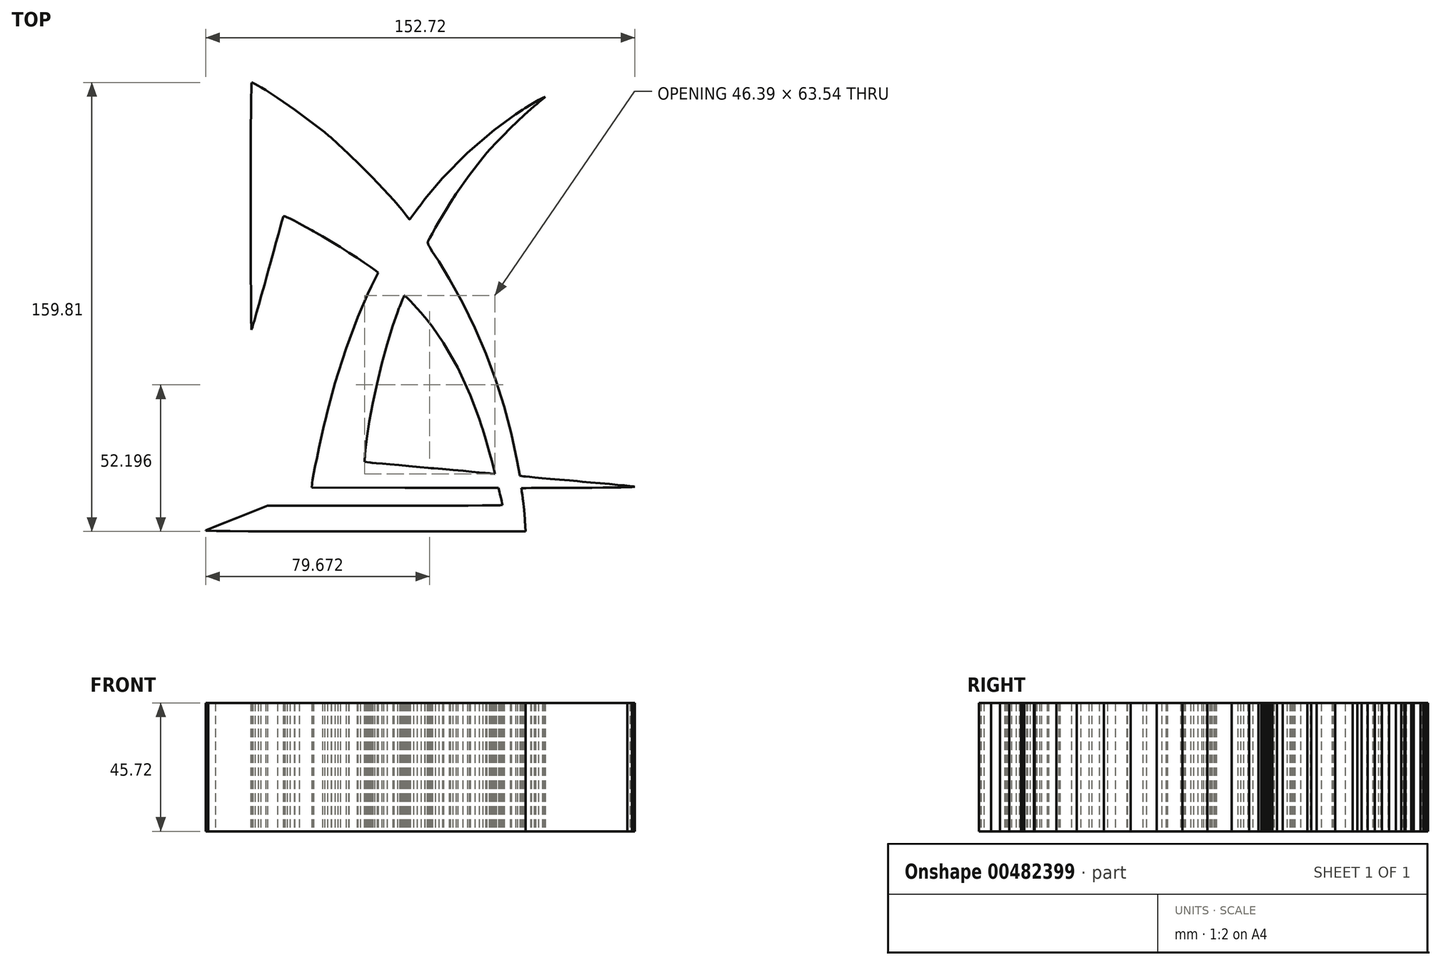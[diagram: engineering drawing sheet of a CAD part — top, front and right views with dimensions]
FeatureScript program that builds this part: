
annotation { "Feature Type Name" : "Feature", "Feature Type Description" : "" }
export const myFeature = defineFeature(function(context is Context, id is Id, definition is map)
    precondition{}
    {
        {
            var Q0;
            Q0=qCreatedBy(makeId("Top.planeOp"),FACE);
            var sketch = newSketch(context, id + "F0", { "sketchPlane" : qUnion([Q0])});
            skLineSegment(sketch, "E0", {"start": v(-90.31, 0) * mm, "end": v(-90.31, -90.31) * mm});
            skLineSegment(sketch, "E1", {"start": v(-90.31, -90.31) * mm, "end": v(90.31, -90.31) * mm});
            skLineSegment(sketch, "E2", {"start": v(90.31, -90.31) * mm, "end": v(90.31, 90.31) * mm});
            skLineSegment(sketch, "E3", {"start": v(90.31, 90.31) * mm, "end": v(-90.31, 90.31) * mm});
            skLineSegment(sketch, "E4", {"start": v(-90.31, 90.31) * mm, "end": v(-90.31, 0) * mm});
            skLineSegment(sketch, "E5", {"start": v(-57.9, 75.78) * mm, "end": v(-56.43, 74.9) * mm});
            skLineSegment(sketch, "E6", {"start": v(-56.43, 74.9) * mm, "end": v(-52.15, 72.16) * mm});
            skLineSegment(sketch, "E7", {"start": v(-52.15, 72.16) * mm, "end": v(-46.09, 67.98) * mm});
            skLineSegment(sketch, "E8", {"start": v(-46.09, 67.98) * mm, "end": v(-39.97, 63.43) * mm});
            skLineSegment(sketch, "E9", {"start": v(-39.97, 63.43) * mm, "end": v(-35.5, 59.91) * mm});
            skLineSegment(sketch, "E10", {"start": v(-35.5, 59.91) * mm, "end": v(-34.04, 58.7) * mm});
            skLineSegment(sketch, "E11", {"start": v(-34.04, 58.7) * mm, "end": v(-33.2, 58) * mm});
            skLineSegment(sketch, "E12", {"start": v(-33.2, 58) * mm, "end": v(-30.73, 55.82) * mm});
            skLineSegment(sketch, "E13", {"start": v(-30.73, 55.82) * mm, "end": v(-26.88, 52.22) * mm});
            skLineSegment(sketch, "E14", {"start": v(-26.88, 52.22) * mm, "end": v(-22.73, 48.17) * mm});
            skLineSegment(sketch, "E15", {"start": v(-22.73, 48.17) * mm, "end": v(-18.52, 43.9) * mm});
            skLineSegment(sketch, "E16", {"start": v(-18.52, 43.9) * mm, "end": v(-14.48, 39.65) * mm});
            skLineSegment(sketch, "E17", {"start": v(-14.48, 39.65) * mm, "end": v(-10.86, 35.68) * mm});
            skLineSegment(sketch, "E18", {"start": v(-10.86, 35.68) * mm, "end": v(-7.9, 32.24) * mm});
            skLineSegment(sketch, "E19", {"start": v(-7.9, 32.24) * mm, "end": v(-6.3, 30.26) * mm});
            skLineSegment(sketch, "E20", {"start": v(-6.3, 30.26) * mm, "end": v(-5.82, 29.56) * mm});
            skLineSegment(sketch, "E21", {"start": v(-5.82, 29.56) * mm, "end": v(-5.75, 29.46) * mm});
            skLineSegment(sketch, "E22", {"start": v(-5.75, 29.46) * mm, "end": v(-5.42, 29.07) * mm});
            skLineSegment(sketch, "E23", {"start": v(-5.42, 29.07) * mm, "end": v(-5.17, 28.94) * mm});
            skLineSegment(sketch, "E24", {"start": v(-5.17, 28.94) * mm, "end": v(-5.15, 28.96) * mm});
            skLineSegment(sketch, "E25", {"start": v(-5.15, 28.96) * mm, "end": v(-5.13, 28.98) * mm});
            skLineSegment(sketch, "E26", {"start": v(-5.13, 28.98) * mm, "end": v(-4.83, 29.38) * mm});
            skLineSegment(sketch, "E27", {"start": v(-4.83, 29.38) * mm, "end": v(-4.04, 30.41) * mm});
            skLineSegment(sketch, "E28", {"start": v(-4.04, 30.41) * mm, "end": v(-2.92, 31.9) * mm});
            skLineSegment(sketch, "E29", {"start": v(-2.92, 31.9) * mm, "end": v(-1.92, 33.24) * mm});
            skLineSegment(sketch, "E30", {"start": v(-1.92, 33.24) * mm, "end": v(-1.59, 33.7) * mm});
            skLineSegment(sketch, "E31", {"start": v(-1.59, 33.7) * mm, "end": v(0.32, 36.23) * mm});
            skLineSegment(sketch, "E32", {"start": v(0.32, 36.23) * mm, "end": v(6.48, 43.52) * mm});
            skLineSegment(sketch, "E33", {"start": v(6.48, 43.52) * mm, "end": v(15.33, 52.55) * mm});
            skLineSegment(sketch, "E34", {"start": v(15.33, 52.55) * mm, "end": v(24.9, 60.71) * mm});
            skLineSegment(sketch, "E35", {"start": v(24.9, 60.71) * mm, "end": v(32.47, 66.26) * mm});
            skLineSegment(sketch, "E36", {"start": v(32.47, 66.26) * mm, "end": v(35.1, 67.95) * mm});
            skLineSegment(sketch, "E37", {"start": v(35.1, 67.95) * mm, "end": v(35.85, 68.43) * mm});
            skLineSegment(sketch, "E38", {"start": v(35.85, 68.43) * mm, "end": v(38.13, 69.85) * mm});
            skLineSegment(sketch, "E39", {"start": v(38.13, 69.85) * mm, "end": v(40.66, 71.37) * mm});
            skLineSegment(sketch, "E40", {"start": v(40.66, 71.37) * mm, "end": v(42.4, 72.33) * mm});
            skLineSegment(sketch, "E41", {"start": v(42.4, 72.33) * mm, "end": v(43.04, 72.57) * mm});
            skLineSegment(sketch, "E42", {"start": v(43.04, 72.57) * mm, "end": v(43.04, 72.5) * mm});
            skLineSegment(sketch, "E43", {"start": v(43.04, 72.5) * mm, "end": v(42.77, 72.28) * mm});
            skLineSegment(sketch, "E44", {"start": v(42.77, 72.28) * mm, "end": v(42.03, 71.63) * mm});
            skLineSegment(sketch, "E45", {"start": v(42.03, 71.63) * mm, "end": v(40.94, 70.72) * mm});
            skLineSegment(sketch, "E46", {"start": v(40.94, 70.72) * mm, "end": v(39.95, 69.9) * mm});
            skLineSegment(sketch, "E47", {"start": v(39.95, 69.9) * mm, "end": v(39.62, 69.64) * mm});
            skLineSegment(sketch, "E48", {"start": v(39.62, 69.64) * mm, "end": v(39.16, 69.28) * mm});
            skLineSegment(sketch, "E49", {"start": v(39.16, 69.28) * mm, "end": v(37.83, 68.13) * mm});
            skLineSegment(sketch, "E50", {"start": v(37.83, 68.13) * mm, "end": v(35.63, 66.15) * mm});
            skLineSegment(sketch, "E51", {"start": v(35.63, 66.15) * mm, "end": v(33.17, 63.82) * mm});
            skLineSegment(sketch, "E52", {"start": v(33.17, 63.82) * mm, "end": v(30.58, 61.3) * mm});
            skLineSegment(sketch, "E53", {"start": v(30.58, 61.3) * mm, "end": v(28, 58.72) * mm});
            skLineSegment(sketch, "E54", {"start": v(28, 58.72) * mm, "end": v(25.6, 56.22) * mm});
            skLineSegment(sketch, "E55", {"start": v(25.6, 56.22) * mm, "end": v(23.5, 53.94) * mm});
            skLineSegment(sketch, "E56", {"start": v(23.5, 53.94) * mm, "end": v(22.24, 52.52) * mm});
            skLineSegment(sketch, "E57", {"start": v(22.24, 52.52) * mm, "end": v(21.84, 52.03) * mm});
            skLineSegment(sketch, "E58", {"start": v(21.84, 52.03) * mm, "end": v(20.82, 50.83) * mm});
            skLineSegment(sketch, "E59", {"start": v(20.82, 50.83) * mm, "end": v(15.98, 44.6) * mm});
            skLineSegment(sketch, "E60", {"start": v(15.98, 44.6) * mm, "end": v(11.35, 38) * mm});
            skLineSegment(sketch, "E61", {"start": v(11.35, 38) * mm, "end": v(10.44, 36.62) * mm});
            skLineSegment(sketch, "E62", {"start": v(10.44, 36.62) * mm, "end": v(10.14, 36.16) * mm});
            skLineSegment(sketch, "E63", {"start": v(10.14, 36.16) * mm, "end": v(9.26, 34.75) * mm});
            skLineSegment(sketch, "E64", {"start": v(9.26, 34.75) * mm, "end": v(7.94, 32.63) * mm});
            skLineSegment(sketch, "E65", {"start": v(7.94, 32.63) * mm, "end": v(6.58, 30.36) * mm});
            skLineSegment(sketch, "E66", {"start": v(6.58, 30.36) * mm, "end": v(5.23, 28.07) * mm});
            skLineSegment(sketch, "E67", {"start": v(5.23, 28.07) * mm, "end": v(3.96, 25.89) * mm});
            skLineSegment(sketch, "E68", {"start": v(3.96, 25.89) * mm, "end": v(2.86, 23.93) * mm});
            skLineSegment(sketch, "E69", {"start": v(2.86, 23.93) * mm, "end": v(1.98, 22.31) * mm});
            skLineSegment(sketch, "E70", {"start": v(1.98, 22.31) * mm, "end": v(1.54, 21.46) * mm});
            skLineSegment(sketch, "E71", {"start": v(1.54, 21.46) * mm, "end": v(1.41, 21.17) * mm});
            skLineSegment(sketch, "E72", {"start": v(1.41, 21.17) * mm, "end": v(1.38, 21.1) * mm});
            skLineSegment(sketch, "E73", {"start": v(1.38, 21.1) * mm, "end": v(1.3, 20.87) * mm});
            skLineSegment(sketch, "E74", {"start": v(1.3, 20.87) * mm, "end": v(1.28, 20.57) * mm});
            skLineSegment(sketch, "E75", {"start": v(1.28, 20.57) * mm, "end": v(1.35, 20.2) * mm});
            skLineSegment(sketch, "E76", {"start": v(1.35, 20.2) * mm, "end": v(1.53, 19.75) * mm});
            skLineSegment(sketch, "E77", {"start": v(1.53, 19.75) * mm, "end": v(1.84, 19.15) * mm});
            skLineSegment(sketch, "E78", {"start": v(1.84, 19.15) * mm, "end": v(2.31, 18.36) * mm});
            skLineSegment(sketch, "E79", {"start": v(2.31, 18.36) * mm, "end": v(2.96, 17.34) * mm});
            skLineSegment(sketch, "E80", {"start": v(2.96, 17.34) * mm, "end": v(3.6, 16.37) * mm});
            skLineSegment(sketch, "E81", {"start": v(3.6, 16.37) * mm, "end": v(3.81, 16.05) * mm});
            skLineSegment(sketch, "E82", {"start": v(3.81, 16.05) * mm, "end": v(5.15, 14.01) * mm});
            skLineSegment(sketch, "E83", {"start": v(5.15, 14.01) * mm, "end": v(8.95, 7.75) * mm});
            skLineSegment(sketch, "E84", {"start": v(8.95, 7.75) * mm, "end": v(13.7, -0.87) * mm});
            skLineSegment(sketch, "E85", {"start": v(13.7, -0.87) * mm, "end": v(18.02, -9.76) * mm});
            skLineSegment(sketch, "E86", {"start": v(18.02, -9.76) * mm, "end": v(21.93, -18.9) * mm});
            skLineSegment(sketch, "E87", {"start": v(21.93, -18.9) * mm, "end": v(25.4, -28.23) * mm});
            skLineSegment(sketch, "E88", {"start": v(25.4, -28.23) * mm, "end": v(28.42, -37.72) * mm});
            skLineSegment(sketch, "E89", {"start": v(28.42, -37.72) * mm, "end": v(30.96, -47.34) * mm});
            skLineSegment(sketch, "E90", {"start": v(30.96, -47.34) * mm, "end": v(32.57, -54.6) * mm});
            skLineSegment(sketch, "E91", {"start": v(32.57, -54.6) * mm, "end": v(33.02, -57.04) * mm});
            skLineSegment(sketch, "E92", {"start": v(33.02, -57.04) * mm, "end": v(34, -62.37) * mm});
            skLineSegment(sketch, "E93", {"start": v(34, -62.37) * mm, "end": v(35.45, -62.58) * mm});
            skLineSegment(sketch, "E94", {"start": v(35.45, -62.58) * mm, "end": v(35.62, -62.6) * mm});
            skLineSegment(sketch, "E95", {"start": v(35.62, -62.6) * mm, "end": v(36.11, -62.65) * mm});
            skLineSegment(sketch, "E96", {"start": v(36.11, -62.65) * mm, "end": v(37.46, -62.78) * mm});
            skLineSegment(sketch, "E97", {"start": v(37.46, -62.78) * mm, "end": v(39.41, -62.97) * mm});
            skLineSegment(sketch, "E98", {"start": v(39.41, -62.97) * mm, "end": v(41.89, -63.19) * mm});
            skLineSegment(sketch, "E99", {"start": v(41.89, -63.19) * mm, "end": v(44.8, -63.45) * mm});
            skLineSegment(sketch, "E100", {"start": v(44.8, -63.45) * mm, "end": v(48.08, -63.74) * mm});
            skLineSegment(sketch, "E101", {"start": v(48.08, -63.74) * mm, "end": v(51.63, -64.06) * mm});
            skLineSegment(sketch, "E102", {"start": v(51.63, -64.06) * mm, "end": v(54.45, -64.3) * mm});
            skLineSegment(sketch, "E103", {"start": v(54.45, -64.3) * mm, "end": v(55.39, -64.38) * mm});
            skLineSegment(sketch, "E104", {"start": v(55.39, -64.38) * mm, "end": v(56.32, -64.46) * mm});
            skLineSegment(sketch, "E105", {"start": v(56.32, -64.46) * mm, "end": v(59.13, -64.7) * mm});
            skLineSegment(sketch, "E106", {"start": v(59.13, -64.7) * mm, "end": v(62.67, -65.03) * mm});
            skLineSegment(sketch, "E107", {"start": v(62.67, -65.03) * mm, "end": v(65.91, -65.32) * mm});
            skLineSegment(sketch, "E108", {"start": v(65.91, -65.32) * mm, "end": v(68.79, -65.6) * mm});
            skLineSegment(sketch, "E109", {"start": v(68.79, -65.6) * mm, "end": v(71.2, -65.84) * mm});
            skLineSegment(sketch, "E110", {"start": v(71.2, -65.84) * mm, "end": v(73.1, -66.04) * mm});
            skLineSegment(sketch, "E111", {"start": v(73.1, -66.04) * mm, "end": v(74.38, -66.19) * mm});
            skLineSegment(sketch, "E112", {"start": v(74.38, -66.19) * mm, "end": v(74.82, -66.24) * mm});
            skLineSegment(sketch, "E113", {"start": v(74.82, -66.24) * mm, "end": v(74.97, -66.29) * mm});
            skLineSegment(sketch, "E114", {"start": v(74.97, -66.29) * mm, "end": v(74.8, -66.35) * mm});
            skLineSegment(sketch, "E115", {"start": v(74.8, -66.35) * mm, "end": v(73.9, -66.41) * mm});
            skLineSegment(sketch, "E116", {"start": v(73.9, -66.41) * mm, "end": v(72.28, -66.47) * mm});
            skLineSegment(sketch, "E117", {"start": v(72.28, -66.47) * mm, "end": v(70, -66.52) * mm});
            skLineSegment(sketch, "E118", {"start": v(70, -66.52) * mm, "end": v(67.13, -66.56) * mm});
            skLineSegment(sketch, "E119", {"start": v(67.13, -66.56) * mm, "end": v(63.68, -66.6) * mm});
            skLineSegment(sketch, "E120", {"start": v(63.68, -66.6) * mm, "end": v(59.73, -66.62) * mm});
            skLineSegment(sketch, "E121", {"start": v(59.73, -66.62) * mm, "end": v(56.42, -66.64) * mm});
            skLineSegment(sketch, "E122", {"start": v(56.42, -66.64) * mm, "end": v(55.32, -66.64) * mm});
            skLineSegment(sketch, "E123", {"start": v(55.32, -66.64) * mm, "end": v(54.27, -66.64) * mm});
            skLineSegment(sketch, "E124", {"start": v(54.27, -66.64) * mm, "end": v(51.14, -66.65) * mm});
            skLineSegment(sketch, "E125", {"start": v(51.14, -66.65) * mm, "end": v(47.25, -66.67) * mm});
            skLineSegment(sketch, "E126", {"start": v(47.25, -66.67) * mm, "end": v(43.73, -66.68) * mm});
            skLineSegment(sketch, "E127", {"start": v(43.73, -66.68) * mm, "end": v(40.66, -66.7) * mm});
            skLineSegment(sketch, "E128", {"start": v(40.66, -66.7) * mm, "end": v(38.12, -66.71) * mm});
            skLineSegment(sketch, "E129", {"start": v(38.12, -66.71) * mm, "end": v(36.2, -66.73) * mm});
            skLineSegment(sketch, "E130", {"start": v(36.2, -66.73) * mm, "end": v(35, -66.75) * mm});
            skLineSegment(sketch, "E131", {"start": v(35, -66.75) * mm, "end": v(34.57, -66.77) * mm});
            skLineSegment(sketch, "E132", {"start": v(34.57, -66.77) * mm, "end": v(34.57, -66.78) * mm});
            skLineSegment(sketch, "E133", {"start": v(34.57, -66.78) * mm, "end": v(34.57, -66.87) * mm});
            skLineSegment(sketch, "E134", {"start": v(34.57, -66.87) * mm, "end": v(34.6, -67.13) * mm});
            skLineSegment(sketch, "E135", {"start": v(34.6, -67.13) * mm, "end": v(34.71, -68) * mm});
            skLineSegment(sketch, "E136", {"start": v(34.71, -68) * mm, "end": v(34.87, -69.25) * mm});
            skLineSegment(sketch, "E137", {"start": v(34.87, -69.25) * mm, "end": v(35.02, -70.39) * mm});
            skLineSegment(sketch, "E138", {"start": v(35.02, -70.39) * mm, "end": v(35.07, -70.77) * mm});
            skLineSegment(sketch, "E139", {"start": v(35.07, -70.77) * mm, "end": v(35.14, -71.3) * mm});
            skLineSegment(sketch, "E140", {"start": v(35.14, -71.3) * mm, "end": v(35.49, -74.6) * mm});
            skLineSegment(sketch, "E141", {"start": v(35.49, -74.6) * mm, "end": v(35.77, -77.87) * mm});
            skLineSegment(sketch, "E142", {"start": v(35.77, -77.87) * mm, "end": v(35.8, -78.39) * mm});
            skLineSegment(sketch, "E143", {"start": v(35.8, -78.39) * mm, "end": v(36.05, -82.2) * mm});
            skLineSegment(sketch, "E144", {"start": v(36.05, -82.2) * mm, "end": v(-21.03, -82.2) * mm});
            skLineSegment(sketch, "E145", {"start": v(-21.03, -82.2) * mm, "end": v(-24.16, -82.2) * mm});
            skLineSegment(sketch, "E146", {"start": v(-24.16, -82.2) * mm, "end": v(-33.54, -82.2) * mm});
            skLineSegment(sketch, "E147", {"start": v(-33.54, -82.2) * mm, "end": v(-44.71, -82.17) * mm});
            skLineSegment(sketch, "E148", {"start": v(-44.71, -82.17) * mm, "end": v(-54.44, -82.14) * mm});
            skLineSegment(sketch, "E149", {"start": v(-54.44, -82.14) * mm, "end": v(-62.62, -82.1) * mm});
            skLineSegment(sketch, "E150", {"start": v(-62.62, -82.1) * mm, "end": v(-69.14, -82.06) * mm});
            skLineSegment(sketch, "E151", {"start": v(-69.14, -82.06) * mm, "end": v(-73.9, -82) * mm});
            skLineSegment(sketch, "E152", {"start": v(-73.9, -82) * mm, "end": v(-76.81, -81.94) * mm});
            skLineSegment(sketch, "E153", {"start": v(-76.81, -81.94) * mm, "end": v(-77.75, -81.88) * mm});
            skLineSegment(sketch, "E154", {"start": v(-77.75, -81.88) * mm, "end": v(-77.7, -81.84) * mm});
            skLineSegment(sketch, "E155", {"start": v(-77.7, -81.84) * mm, "end": v(-76.77, -81.42) * mm});
            skLineSegment(sketch, "E156", {"start": v(-76.77, -81.42) * mm, "end": v(-74.33, -80.4) * mm});
            skLineSegment(sketch, "E157", {"start": v(-74.33, -80.4) * mm, "end": v(-70.8, -78.97) * mm});
            skLineSegment(sketch, "E158", {"start": v(-70.8, -78.97) * mm, "end": v(-67.63, -77.7) * mm});
            skLineSegment(sketch, "E159", {"start": v(-67.63, -77.7) * mm, "end": v(-66.57, -77.3) * mm});
            skLineSegment(sketch, "E160", {"start": v(-66.57, -77.3) * mm, "end": v(-55.7, -73.02) * mm});
            skLineSegment(sketch, "E161", {"start": v(-55.7, -73.02) * mm, "end": v(-13.9, -73.02) * mm});
            skLineSegment(sketch, "E162", {"start": v(-13.9, -73.02) * mm, "end": v(-11.8, -73.02) * mm});
            skLineSegment(sketch, "E163", {"start": v(-11.8, -73.02) * mm, "end": v(-5.51, -73.02) * mm});
            skLineSegment(sketch, "E164", {"start": v(-5.51, -73.02) * mm, "end": v(2.32, -73) * mm});
            skLineSegment(sketch, "E165", {"start": v(2.32, -73) * mm, "end": v(9.4, -72.99) * mm});
            skLineSegment(sketch, "E166", {"start": v(9.4, -72.99) * mm, "end": v(15.6, -72.96) * mm});
            skLineSegment(sketch, "E167", {"start": v(15.6, -72.96) * mm, "end": v(20.7, -72.93) * mm});
            skLineSegment(sketch, "E168", {"start": v(20.7, -72.93) * mm, "end": v(24.57, -72.89) * mm});
            skLineSegment(sketch, "E169", {"start": v(24.57, -72.89) * mm, "end": v(27.02, -72.85) * mm});
            skLineSegment(sketch, "E170", {"start": v(27.02, -72.85) * mm, "end": v(27.87, -72.82) * mm});
            skLineSegment(sketch, "E171", {"start": v(27.87, -72.82) * mm, "end": v(27.87, -72.81) * mm});
            skLineSegment(sketch, "E172", {"start": v(27.87, -72.81) * mm, "end": v(27.87, -72.75) * mm});
            skLineSegment(sketch, "E173", {"start": v(27.87, -72.75) * mm, "end": v(27.83, -72.57) * mm});
            skLineSegment(sketch, "E174", {"start": v(27.83, -72.57) * mm, "end": v(27.73, -72.07) * mm});
            skLineSegment(sketch, "E175", {"start": v(27.73, -72.07) * mm, "end": v(27.57, -71.38) * mm});
            skLineSegment(sketch, "E176", {"start": v(27.57, -71.38) * mm, "end": v(27.43, -70.79) * mm});
            skLineSegment(sketch, "E177", {"start": v(27.43, -70.79) * mm, "end": v(27.38, -70.6) * mm});
            skLineSegment(sketch, "E178", {"start": v(27.38, -70.6) * mm, "end": v(27.32, -70.38) * mm});
            skLineSegment(sketch, "E179", {"start": v(27.32, -70.38) * mm, "end": v(27.16, -69.75) * mm});
            skLineSegment(sketch, "E180", {"start": v(27.16, -69.75) * mm, "end": v(26.96, -68.91) * mm});
            skLineSegment(sketch, "E181", {"start": v(26.96, -68.91) * mm, "end": v(26.78, -68.19) * mm});
            skLineSegment(sketch, "E182", {"start": v(26.78, -68.19) * mm, "end": v(26.7, -67.8) * mm});
            skLineSegment(sketch, "E183", {"start": v(26.7, -67.8) * mm, "end": v(26.67, -67.66) * mm});
            skLineSegment(sketch, "E184", {"start": v(26.67, -67.66) * mm, "end": v(26.46, -66.67) * mm});
            skLineSegment(sketch, "E185", {"start": v(26.46, -66.67) * mm, "end": v(-6.8, -66.6) * mm});
            skLineSegment(sketch, "E186", {"start": v(-6.8, -66.6) * mm, "end": v(-40.04, -66.5) * mm});
            skLineSegment(sketch, "E187", {"start": v(-40.04, -66.5) * mm, "end": v(-39.93, -65.26) * mm});
            skLineSegment(sketch, "E188", {"start": v(-39.93, -65.26) * mm, "end": v(-39.9, -64.93) * mm});
            skLineSegment(sketch, "E189", {"start": v(-39.9, -64.93) * mm, "end": v(-39.73, -63.92) * mm});
            skLineSegment(sketch, "E190", {"start": v(-39.73, -63.92) * mm, "end": v(-39.35, -61.77) * mm});
            skLineSegment(sketch, "E191", {"start": v(-39.35, -61.77) * mm, "end": v(-38.8, -59.01) * mm});
            skLineSegment(sketch, "E192", {"start": v(-38.8, -59.01) * mm, "end": v(-38.16, -55.83) * mm});
            skLineSegment(sketch, "E193", {"start": v(-38.16, -55.83) * mm, "end": v(-37.44, -52.4) * mm});
            skLineSegment(sketch, "E194", {"start": v(-37.44, -52.4) * mm, "end": v(-36.68, -48.95) * mm});
            skLineSegment(sketch, "E195", {"start": v(-36.68, -48.95) * mm, "end": v(-35.94, -45.65) * mm});
            skLineSegment(sketch, "E196", {"start": v(-35.94, -45.65) * mm, "end": v(-35.42, -43.42) * mm});
            skLineSegment(sketch, "E197", {"start": v(-35.42, -43.42) * mm, "end": v(-35.24, -42.69) * mm});
            skLineSegment(sketch, "E198", {"start": v(-35.24, -42.69) * mm, "end": v(-34.43, -39.34) * mm});
            skLineSegment(sketch, "E199", {"start": v(-34.43, -39.34) * mm, "end": v(-31.73, -29.36) * mm});
            skLineSegment(sketch, "E200", {"start": v(-31.73, -29.36) * mm, "end": v(-27.88, -17.17) * mm});
            skLineSegment(sketch, "E201", {"start": v(-27.88, -17.17) * mm, "end": v(-23.6, -5.8) * mm});
            skLineSegment(sketch, "E202", {"start": v(-23.6, -5.8) * mm, "end": v(-20.05, 2.37) * mm});
            skLineSegment(sketch, "E203", {"start": v(-20.05, 2.37) * mm, "end": v(-18.77, 5.05) * mm});
            skLineSegment(sketch, "E204", {"start": v(-18.77, 5.05) * mm, "end": v(-16.44, 9.95) * mm});
            skLineSegment(sketch, "E205", {"start": v(-16.44, 9.95) * mm, "end": v(-17.29, 10.62) * mm});
            skLineSegment(sketch, "E206", {"start": v(-17.29, 10.62) * mm, "end": v(-17.72, 10.96) * mm});
            skLineSegment(sketch, "E207", {"start": v(-17.72, 10.96) * mm, "end": v(-19.05, 11.94) * mm});
            skLineSegment(sketch, "E208", {"start": v(-19.05, 11.94) * mm, "end": v(-21.28, 13.49) * mm});
            skLineSegment(sketch, "E209", {"start": v(-21.28, 13.49) * mm, "end": v(-23.88, 15.22) * mm});
            skLineSegment(sketch, "E210", {"start": v(-23.88, 15.22) * mm, "end": v(-26.76, 17.08) * mm});
            skLineSegment(sketch, "E211", {"start": v(-26.76, 17.08) * mm, "end": v(-29.84, 19) * mm});
            skLineSegment(sketch, "E212", {"start": v(-29.84, 19) * mm, "end": v(-33.02, 20.94) * mm});
            skLineSegment(sketch, "E213", {"start": v(-33.02, 20.94) * mm, "end": v(-36.21, 22.84) * mm});
            skLineSegment(sketch, "E214", {"start": v(-36.21, 22.84) * mm, "end": v(-38.55, 24.18) * mm});
            skLineSegment(sketch, "E215", {"start": v(-38.55, 24.18) * mm, "end": v(-39.33, 24.62) * mm});
            skLineSegment(sketch, "E216", {"start": v(-39.33, 24.62) * mm, "end": v(-40.03, 25.01) * mm});
            skLineSegment(sketch, "E217", {"start": v(-40.03, 25.01) * mm, "end": v(-42.12, 26.18) * mm});
            skLineSegment(sketch, "E218", {"start": v(-42.12, 26.18) * mm, "end": v(-44.43, 27.44) * mm});
            skLineSegment(sketch, "E219", {"start": v(-44.43, 27.44) * mm, "end": v(-46.28, 28.43) * mm});
            skLineSegment(sketch, "E220", {"start": v(-46.28, 28.43) * mm, "end": v(-47.73, 29.16) * mm});
            skLineSegment(sketch, "E221", {"start": v(-47.73, 29.16) * mm, "end": v(-48.8, 29.65) * mm});
            skLineSegment(sketch, "E222", {"start": v(-48.8, 29.65) * mm, "end": v(-49.55, 29.92) * mm});
            skLineSegment(sketch, "E223", {"start": v(-49.55, 29.92) * mm, "end": v(-50, 30) * mm});
            skLineSegment(sketch, "E224", {"start": v(-50, 30) * mm, "end": v(-50.19, 29.92) * mm});
            skLineSegment(sketch, "E225", {"start": v(-50.19, 29.92) * mm, "end": v(-50.2, 29.88) * mm});
            skLineSegment(sketch, "E226", {"start": v(-50.2, 29.88) * mm, "end": v(-50.22, 29.82) * mm});
            skLineSegment(sketch, "E227", {"start": v(-50.22, 29.82) * mm, "end": v(-50.34, 29.39) * mm});
            skLineSegment(sketch, "E228", {"start": v(-50.34, 29.39) * mm, "end": v(-50.68, 28.15) * mm});
            skLineSegment(sketch, "E229", {"start": v(-50.68, 28.15) * mm, "end": v(-51.2, 26.25) * mm});
            skLineSegment(sketch, "E230", {"start": v(-51.2, 26.25) * mm, "end": v(-51.89, 23.77) * mm});
            skLineSegment(sketch, "E231", {"start": v(-51.89, 23.77) * mm, "end": v(-52.7, 20.8) * mm});
            skLineSegment(sketch, "E232", {"start": v(-52.7, 20.8) * mm, "end": v(-53.63, 17.4) * mm});
            skLineSegment(sketch, "E233", {"start": v(-53.63, 17.4) * mm, "end": v(-54.65, 13.68) * mm});
            skLineSegment(sketch, "E234", {"start": v(-54.65, 13.68) * mm, "end": v(-55.47, 10.7) * mm});
            skLineSegment(sketch, "E235", {"start": v(-55.47, 10.7) * mm, "end": v(-55.74, 9.7) * mm});
            skLineSegment(sketch, "E236", {"start": v(-55.74, 9.7) * mm, "end": v(-56.01, 8.7) * mm});
            skLineSegment(sketch, "E237", {"start": v(-56.01, 8.7) * mm, "end": v(-56.83, 5.73) * mm});
            skLineSegment(sketch, "E238", {"start": v(-56.83, 5.73) * mm, "end": v(-57.86, 2) * mm});
            skLineSegment(sketch, "E239", {"start": v(-57.86, 2) * mm, "end": v(-58.8, -1.38) * mm});
            skLineSegment(sketch, "E240", {"start": v(-58.8, -1.38) * mm, "end": v(-59.64, -4.34) * mm});
            skLineSegment(sketch, "E241", {"start": v(-59.64, -4.34) * mm, "end": v(-60.35, -6.8) * mm});
            skLineSegment(sketch, "E242", {"start": v(-60.35, -6.8) * mm, "end": v(-60.9, -8.69) * mm});
            skLineSegment(sketch, "E243", {"start": v(-60.9, -8.69) * mm, "end": v(-61.28, -9.9) * mm});
            skLineSegment(sketch, "E244", {"start": v(-61.28, -9.9) * mm, "end": v(-61.4, -10.33) * mm});
            skLineSegment(sketch, "E245", {"start": v(-61.4, -10.33) * mm, "end": v(-61.45, -10.37) * mm});
            skLineSegment(sketch, "E246", {"start": v(-61.45, -10.37) * mm, "end": v(-61.5, -9.55) * mm});
            skLineSegment(sketch, "E247", {"start": v(-61.5, -9.55) * mm, "end": v(-61.56, -7.03) * mm});
            skLineSegment(sketch, "E248", {"start": v(-61.56, -7.03) * mm, "end": v(-61.6, -3) * mm});
            skLineSegment(sketch, "E249", {"start": v(-61.6, -3) * mm, "end": v(-61.65, 2.34) * mm});
            skLineSegment(sketch, "E250", {"start": v(-61.65, 2.34) * mm, "end": v(-61.69, 8.84) * mm});
            skLineSegment(sketch, "E251", {"start": v(-61.69, 8.84) * mm, "end": v(-61.71, 16.31) * mm});
            skLineSegment(sketch, "E252", {"start": v(-61.71, 16.31) * mm, "end": v(-61.73, 24.57) * mm});
            skLineSegment(sketch, "E253", {"start": v(-61.73, 24.57) * mm, "end": v(-61.74, 31.23) * mm});
            skLineSegment(sketch, "E254", {"start": v(-61.74, 31.23) * mm, "end": v(-61.74, 33.44) * mm});
            skLineSegment(sketch, "E255", {"start": v(-61.74, 33.44) * mm, "end": v(-61.74, 36.23) * mm});
            skLineSegment(sketch, "E256", {"start": v(-61.74, 36.23) * mm, "end": v(-61.73, 44.57) * mm});
            skLineSegment(sketch, "E257", {"start": v(-61.73, 44.57) * mm, "end": v(-61.72, 53.9) * mm});
            skLineSegment(sketch, "E258", {"start": v(-61.72, 53.9) * mm, "end": v(-61.69, 61.54) * mm});
            skLineSegment(sketch, "E259", {"start": v(-61.69, 61.54) * mm, "end": v(-61.65, 67.58) * mm});
            skLineSegment(sketch, "E260", {"start": v(-61.65, 67.58) * mm, "end": v(-61.6, 72.1) * mm});
            skLineSegment(sketch, "E261", {"start": v(-61.6, 72.1) * mm, "end": v(-61.53, 75.23) * mm});
            skLineSegment(sketch, "E262", {"start": v(-61.53, 75.23) * mm, "end": v(-61.45, 77.03) * mm});
            skLineSegment(sketch, "E263", {"start": v(-61.45, 77.03) * mm, "end": v(-61.37, 77.61) * mm});
            skLineSegment(sketch, "E264", {"start": v(-61.37, 77.61) * mm, "end": v(-61.35, 77.61) * mm});
            skLineSegment(sketch, "E265", {"start": v(-61.35, 77.61) * mm, "end": v(-61.25, 77.61) * mm});
            skLineSegment(sketch, "E266", {"start": v(-61.25, 77.61) * mm, "end": v(-60.96, 77.47) * mm});
            skLineSegment(sketch, "E267", {"start": v(-60.96, 77.47) * mm, "end": v(-60.18, 77.08) * mm});
            skLineSegment(sketch, "E268", {"start": v(-60.18, 77.08) * mm, "end": v(-59.12, 76.5) * mm});
            skLineSegment(sketch, "E269", {"start": v(-59.12, 76.5) * mm, "end": v(-58.2, 75.96) * mm});
            skLineSegment(sketch, "E270", {"start": v(-58.2, 75.96) * mm, "end": v(-57.9, 75.78) * mm});
            skLineSegment(sketch, "E271", {"start": v(-9, -2.72) * mm, "end": v(-9.56, -4.26) * mm});
            skLineSegment(sketch, "E272", {"start": v(-9.56, -4.26) * mm, "end": v(-11.13, -8.94) * mm});
            skLineSegment(sketch, "E273", {"start": v(-11.13, -8.94) * mm, "end": v(-13.17, -15.6) * mm});
            skLineSegment(sketch, "E274", {"start": v(-13.17, -15.6) * mm, "end": v(-15.08, -22.52) * mm});
            skLineSegment(sketch, "E275", {"start": v(-15.08, -22.52) * mm, "end": v(-16.8, -29.52) * mm});
            skLineSegment(sketch, "E276", {"start": v(-16.8, -29.52) * mm, "end": v(-18.3, -36.42) * mm});
            skLineSegment(sketch, "E277", {"start": v(-18.3, -36.42) * mm, "end": v(-19.54, -43.04) * mm});
            skLineSegment(sketch, "E278", {"start": v(-19.54, -43.04) * mm, "end": v(-20.48, -49.2) * mm});
            skLineSegment(sketch, "E279", {"start": v(-20.48, -49.2) * mm, "end": v(-20.95, -53.33) * mm});
            skLineSegment(sketch, "E280", {"start": v(-20.95, -53.33) * mm, "end": v(-21.06, -54.72) * mm});
            skLineSegment(sketch, "E281", {"start": v(-21.06, -54.72) * mm, "end": v(-21.27, -57.4) * mm});
            skLineSegment(sketch, "E282", {"start": v(-21.27, -57.4) * mm, "end": v(-19.37, -57.64) * mm});
            skLineSegment(sketch, "E283", {"start": v(-19.37, -57.64) * mm, "end": v(-19.17, -57.66) * mm});
            skLineSegment(sketch, "E284", {"start": v(-19.17, -57.66) * mm, "end": v(-18.58, -57.72) * mm});
            skLineSegment(sketch, "E285", {"start": v(-18.58, -57.72) * mm, "end": v(-17.05, -57.86) * mm});
            skLineSegment(sketch, "E286", {"start": v(-17.05, -57.86) * mm, "end": v(-14.89, -58.05) * mm});
            skLineSegment(sketch, "E287", {"start": v(-14.89, -58.05) * mm, "end": v(-12.17, -58.3) * mm});
            skLineSegment(sketch, "E288", {"start": v(-12.17, -58.3) * mm, "end": v(-8.98, -58.59) * mm});
            skLineSegment(sketch, "E289", {"start": v(-8.98, -58.59) * mm, "end": v(-5.42, -58.9) * mm});
            skLineSegment(sketch, "E290", {"start": v(-5.42, -58.9) * mm, "end": v(-1.58, -59.25) * mm});
            skLineSegment(sketch, "E291", {"start": v(-1.58, -59.25) * mm, "end": v(1.46, -59.53) * mm});
            skLineSegment(sketch, "E292", {"start": v(1.46, -59.53) * mm, "end": v(2.47, -59.62) * mm});
            skLineSegment(sketch, "E293", {"start": v(2.47, -59.62) * mm, "end": v(3.48, -59.7) * mm});
            skLineSegment(sketch, "E294", {"start": v(3.48, -59.7) * mm, "end": v(6.5, -59.97) * mm});
            skLineSegment(sketch, "E295", {"start": v(6.5, -59.97) * mm, "end": v(10.32, -60.3) * mm});
            skLineSegment(sketch, "E296", {"start": v(10.32, -60.3) * mm, "end": v(13.83, -60.62) * mm});
            skLineSegment(sketch, "E297", {"start": v(13.83, -60.62) * mm, "end": v(16.95, -60.9) * mm});
            skLineSegment(sketch, "E298", {"start": v(16.95, -60.9) * mm, "end": v(19.59, -61.15) * mm});
            skLineSegment(sketch, "E299", {"start": v(19.59, -61.15) * mm, "end": v(21.66, -61.34) * mm});
            skLineSegment(sketch, "E300", {"start": v(21.66, -61.34) * mm, "end": v(23.09, -61.48) * mm});
            skLineSegment(sketch, "E301", {"start": v(23.09, -61.48) * mm, "end": v(23.6, -61.54) * mm});
            skLineSegment(sketch, "E302", {"start": v(23.6, -61.54) * mm, "end": v(23.78, -61.56) * mm});
            skLineSegment(sketch, "E303", {"start": v(23.78, -61.56) * mm, "end": v(25.12, -61.77) * mm});
            skLineSegment(sketch, "E304", {"start": v(25.12, -61.77) * mm, "end": v(24.9, -60.5) * mm});
            skLineSegment(sketch, "E305", {"start": v(24.9, -60.5) * mm, "end": v(24.8, -59.92) * mm});
            skLineSegment(sketch, "E306", {"start": v(24.8, -59.92) * mm, "end": v(24.26, -57.83) * mm});
            skLineSegment(sketch, "E307", {"start": v(24.26, -57.83) * mm, "end": v(23.16, -53.82) * mm});
            skLineSegment(sketch, "E308", {"start": v(23.16, -53.82) * mm, "end": v(21.8, -49.22) * mm});
            skLineSegment(sketch, "E309", {"start": v(21.8, -49.22) * mm, "end": v(20.78, -45.9) * mm});
            skLineSegment(sketch, "E310", {"start": v(20.78, -45.9) * mm, "end": v(20.43, -44.8) * mm});
            skLineSegment(sketch, "E311", {"start": v(20.43, -44.8) * mm, "end": v(19.5, -41.99) * mm});
            skLineSegment(sketch, "E312", {"start": v(19.5, -41.99) * mm, "end": v(16.36, -33.66) * mm});
            skLineSegment(sketch, "E313", {"start": v(16.36, -33.66) * mm, "end": v(11.87, -23.82) * mm});
            skLineSegment(sketch, "E314", {"start": v(11.87, -23.82) * mm, "end": v(6.87, -15.08) * mm});
            skLineSegment(sketch, "E315", {"start": v(6.87, -15.08) * mm, "end": v(2.74, -9.11) * mm});
            skLineSegment(sketch, "E316", {"start": v(2.74, -9.11) * mm, "end": v(1.23, -7.23) * mm});
            skLineSegment(sketch, "E317", {"start": v(1.23, -7.23) * mm, "end": v(0.95, -6.88) * mm});
            skLineSegment(sketch, "E318", {"start": v(0.95, -6.88) * mm, "end": v(0.09, -5.83) * mm});
            skLineSegment(sketch, "E319", {"start": v(0.09, -5.83) * mm, "end": v(-1.2, -4.34) * mm});
            skLineSegment(sketch, "E320", {"start": v(-1.2, -4.34) * mm, "end": v(-2.52, -2.83) * mm});
            skLineSegment(sketch, "E321", {"start": v(-2.52, -2.83) * mm, "end": v(-3.81, -1.41) * mm});
            skLineSegment(sketch, "E322", {"start": v(-3.81, -1.41) * mm, "end": v(-5, -0.15) * mm});
            skLineSegment(sketch, "E323", {"start": v(-5, -0.15) * mm, "end": v(-5.98, 0.85) * mm});
            skLineSegment(sketch, "E324", {"start": v(-5.98, 0.85) * mm, "end": v(-6.7, 1.52) * mm});
            skLineSegment(sketch, "E325", {"start": v(-6.7, 1.52) * mm, "end": v(-6.97, 1.76) * mm});
            skLineSegment(sketch, "E326", {"start": v(-6.97, 1.76) * mm, "end": v(-7.06, 1.76) * mm});
            skLineSegment(sketch, "E327", {"start": v(-7.06, 1.76) * mm, "end": v(-7.11, 1.76) * mm});
            skLineSegment(sketch, "E328", {"start": v(-7.11, 1.76) * mm, "end": v(-7.29, 1.41) * mm});
            skLineSegment(sketch, "E329", {"start": v(-7.29, 1.41) * mm, "end": v(-7.73, 0.45) * mm});
            skLineSegment(sketch, "E330", {"start": v(-7.73, 0.45) * mm, "end": v(-8.33, -0.97) * mm});
            skLineSegment(sketch, "E331", {"start": v(-8.33, -0.97) * mm, "end": v(-8.83, -2.28) * mm});
            skLineSegment(sketch, "E332", {"start": v(-8.83, -2.28) * mm, "end": v(-9, -2.72) * mm});
            skLineSegment(sketch, "E333", {"start": v(4.1, -34.6) * mm, "end": v(4.74, -34.9) * mm});
            skLineSegment(sketch, "E334", {"start": v(4.74, -34.9) * mm, "end": v(6.5, -36.17) * mm});
            skLineSegment(sketch, "E335", {"start": v(6.5, -36.17) * mm, "end": v(8.25, -38.2) * mm});
            skLineSegment(sketch, "E336", {"start": v(8.25, -38.2) * mm, "end": v(9.34, -40.56) * mm});
            skLineSegment(sketch, "E337", {"start": v(9.34, -40.56) * mm, "end": v(9.76, -43.1) * mm});
            skLineSegment(sketch, "E338", {"start": v(9.76, -43.1) * mm, "end": v(9.5, -45.67) * mm});
            skLineSegment(sketch, "E339", {"start": v(9.5, -45.67) * mm, "end": v(8.57, -48.13) * mm});
            skLineSegment(sketch, "E340", {"start": v(8.57, -48.13) * mm, "end": v(6.96, -50.33) * mm});
            skLineSegment(sketch, "E341", {"start": v(6.96, -50.33) * mm, "end": v(5.28, -51.77) * mm});
            skLineSegment(sketch, "E342", {"start": v(5.28, -51.77) * mm, "end": v(4.66, -52.14) * mm});
            skLineSegment(sketch, "E343", {"start": v(4.66, -52.14) * mm, "end": v(4.42, -52.28) * mm});
            skLineSegment(sketch, "E344", {"start": v(4.42, -52.28) * mm, "end": v(3.7, -52.65) * mm});
            skLineSegment(sketch, "E345", {"start": v(3.7, -52.65) * mm, "end": v(2.78, -52.93) * mm});
            skLineSegment(sketch, "E346", {"start": v(2.78, -52.93) * mm, "end": v(1.64, -53.06) * mm});
            skLineSegment(sketch, "E347", {"start": v(1.64, -53.06) * mm, "end": v(0.4, -53.1) * mm});
            skLineSegment(sketch, "E348", {"start": v(0.4, -53.1) * mm, "end": v(0, -53.1) * mm});
            skLineSegment(sketch, "E349", {"start": v(0, -53.1) * mm, "end": v(-0.41, -53.1) * mm});
            skLineSegment(sketch, "E350", {"start": v(-0.41, -53.1) * mm, "end": v(-1.64, -53.06) * mm});
            skLineSegment(sketch, "E351", {"start": v(-1.64, -53.06) * mm, "end": v(-2.78, -52.93) * mm});
            skLineSegment(sketch, "E352", {"start": v(-2.78, -52.93) * mm, "end": v(-3.7, -52.65) * mm});
            skLineSegment(sketch, "E353", {"start": v(-3.7, -52.65) * mm, "end": v(-4.42, -52.28) * mm});
            skLineSegment(sketch, "E354", {"start": v(-4.42, -52.28) * mm, "end": v(-4.66, -52.14) * mm});
            skLineSegment(sketch, "E355", {"start": v(-4.66, -52.14) * mm, "end": v(-5.3, -51.76) * mm});
            skLineSegment(sketch, "E356", {"start": v(-5.3, -51.76) * mm, "end": v(-6.99, -50.28) * mm});
            skLineSegment(sketch, "E357", {"start": v(-6.99, -50.28) * mm, "end": v(-8.68, -47.96) * mm});
            skLineSegment(sketch, "E358", {"start": v(-8.68, -47.96) * mm, "end": v(-9.64, -45.34) * mm});
            skLineSegment(sketch, "E359", {"start": v(-9.64, -45.34) * mm, "end": v(-9.85, -43.28) * mm});
            skLineSegment(sketch, "E360", {"start": v(-9.85, -43.28) * mm, "end": v(-9.77, -42.62) * mm});
            skLineSegment(sketch, "E361", {"start": v(-9.77, -42.62) * mm, "end": v(-9.7, -42) * mm});
            skLineSegment(sketch, "E362", {"start": v(-9.7, -42) * mm, "end": v(-9.2, -40.21) * mm});
            skLineSegment(sketch, "E363", {"start": v(-9.2, -40.21) * mm, "end": v(-8.12, -38.1) * mm});
            skLineSegment(sketch, "E364", {"start": v(-8.12, -38.1) * mm, "end": v(-6.63, -36.36) * mm});
            skLineSegment(sketch, "E365", {"start": v(-6.63, -36.36) * mm, "end": v(-4.81, -35.01) * mm});
            skLineSegment(sketch, "E366", {"start": v(-4.81, -35.01) * mm, "end": v(-2.75, -34.11) * mm});
            skLineSegment(sketch, "E367", {"start": v(-2.75, -34.11) * mm, "end": v(-0.52, -33.72) * mm});
            skLineSegment(sketch, "E368", {"start": v(-0.52, -33.72) * mm, "end": v(1.79, -33.86) * mm});
            skLineSegment(sketch, "E369", {"start": v(1.79, -33.86) * mm, "end": v(3.55, -34.35) * mm});
            skLineSegment(sketch, "E370", {"start": v(3.55, -34.35) * mm, "end": v(4.1, -34.6) * mm});
            skSolve(sketch);
        }
        {
            var Q0;
            Q0=makeQuery(id+"F0.imprint","IMPRINT",FACE,{"disambiguationData":[TD([[makeQuery(id+"F0.imprint","IMPRINT",EDGE,{"derivedFrom":sQuery(id+"F0.wireOp",EDGE,"E5")}),-1.0]])]});
            extrude(context, id + "F1", {"entities" : qUnion([Q0]), "depth" : 45.72 * mm});
        }
    });
